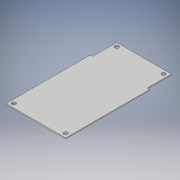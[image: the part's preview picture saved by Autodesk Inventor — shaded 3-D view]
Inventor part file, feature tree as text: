
AUTODESK INVENTOR PART (.ipt)
format: ipt  version: 2018 (Build 220112000, 112)  size: 115,712 bytes
history: native  units: in
note: dims shown in document units (in); Inventor stores cm internally (conversion verified against a paired STEP export)
features: extrude x2, sketch x2
ambient origin geometry x8: Origin, YZ Plane, XZ Plane, XY Plane, X Axis, Y Axis, Z Axis, Center Point
bodies: Solid1 (feature_tree)
feature tree (4):
  extrude  "Extrusion1"  Depth=2.7165in
  extrude  "Extrusion2"  Depth=0.031in
  sketch  "Sketch1"  dims[d0=1.9291in d1=2.7165in]
  sketch  "Sketch2"  dims[d2=1.7717in d3=1.5748in d4=0.031in d5=0.0in d6=0.125in d7=0.125in d16=0.125in d17=0.125in d18=0.125in d19=0.125in d20=0.0in d21=0.0in]
